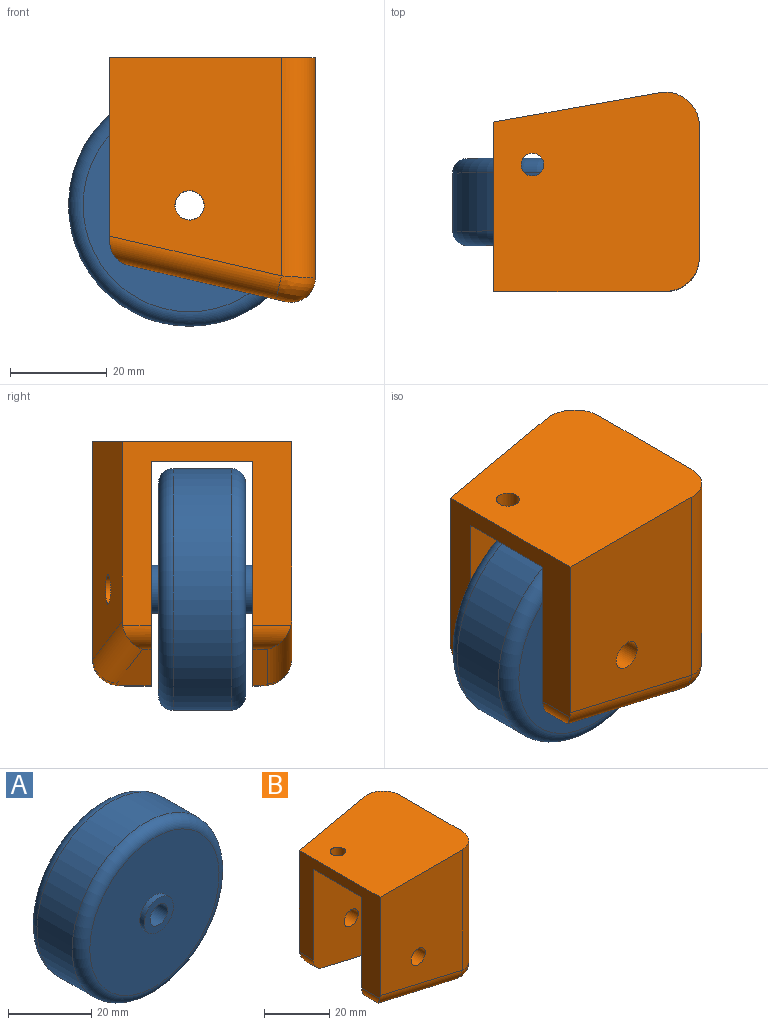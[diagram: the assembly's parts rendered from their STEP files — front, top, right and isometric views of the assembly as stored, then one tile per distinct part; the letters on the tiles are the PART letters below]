
ASSEMBLY  parts=2 mates=1
PART A: 10 faces, bbox 54.1x21x54.1 mm
  f0: cylinder r=25mm len=50mm, axis (0,1,0), area 1885mm2, adj f8,f9
  f1: cylinder r=3mm len=21mm, axis (0,1,0), area 395.8mm2, adj f5,f7
  f2: plane 44x44mm, normal (0,-1,0), area 1442mm2, adj f4,f9
  f3: plane 44x44mm, normal (0,1,0), area 1442mm2, adj f6,f8
  f4: cylinder r=5mm len=10mm, axis (0,1,0), area 47.1mm2, adj f2,f5
  f5: plane 10x10mm, normal (0,-1,0), area 50.3mm2, adj f1,f4
  f6: cylinder r=5mm len=10mm, axis (0,-1,0), area 47.1mm2, adj f3,f7
  f7: plane 10x10mm, normal (0,1,0), area 50.3mm2, adj f1,f6
  f8: torus R=22mm, axis (0,-1,0), area 707.9mm2, adj f0,f3
  f9: torus R=22mm, axis (0,-1,0), area 707.9mm2, adj f0,f2
PART B: 23 faces, bbox 43.9x41.6x52.1 mm
  f0: plane 45.55x27.16mm, normal (1,0,0), area 364.4mm2, adj f1,f3,f4,f5,f6,f10,f15,f19
  f1: cylinder r=7mm len=45.55mm, axis (0,0,-1), area 553.2mm2, adj f0,f2,f10,f16
  f2: plane 45.23x34.51mm, normal (-0.17,0.98,0), area 1398.9mm2, adj f1,f7,f10,f12,f18
  f3: cylinder r=7mm len=45.55mm, axis (0,0,-1), area 498.3mm2, adj f0,f8,f10,f21
  f4: plane 46.55x42.5mm, normal (0,-1,0), area 1782.7mm2, adj f0,f6,f7,f12,f14,f15,f17
  f5: plane 46.55x42.5mm, normal (0,1,0), area 1782.7mm2, adj f0,f6,f7,f11,f13,f19,f20
  f6: plane 42.5x21mm, normal (0,0,-1), area 875.2mm2, adj f0,f4,f5,f7,f9
  f7: plane 38.03x35.01mm, normal (-1,0,0), area 616.3mm2, adj f2,f4,f5,f6,f8,f10,f17,f18
  f8: plane 45.08x35.5mm, normal (0,-1,0), area 1425.4mm2, adj f3,f7,f10,f11,f22
  f9: cylinder r=2.35mm len=4.7mm, axis (0,0,-1), area 59.1mm2, adj f6,f10
  f10: plane 42.5x41.16mm, normal (0,0,1), area 1603.4mm2, adj f0,f1,f2,f3,f7,f8,f9
  f11: cylinder r=3.05mm len=8mm, axis (0,-1,0), area 153.3mm2, adj f5,f8
  f12: cylinder r=3.05mm len=9.45mm, axis (0,-1,0), area 170.8mm2, adj f2,f4
  f13: plane 32.5x7.52mm, normal (-0.23,0,-0.97), area 99.2mm2, adj f5,f19,f20,f21,f22
  f14: plane 32.5x7.52mm, normal (-0.23,0,-0.97), area 154.6mm2, adj f4,f15,f16,f17,f18
  f15: cylinder r=5mm len=6.13mm, axis (0,1,0), area 46.4mm2, adj f0,f4,f14,f16
  f16: bspline ~10.07x7.1mm, area 79.2mm2, adj f1,f14,f15,f18
  f17: cylinder r=5mm len=5.91mm, axis (0,1,0), area 28.4mm2, adj f4,f7,f14,f18
  f18: cylinder r=5mm len=34.81mm, axis (-0.96,-0.17,0.22), area 260.8mm2, adj f2,f7,f14,f16,f17
  f19: cylinder r=5mm len=6.13mm, axis (0,1,0), area 9mm2, adj f0,f5,f13,f21
  f20: cylinder r=5mm len=7.87mm, axis (0,1,0), area 39.5mm2, adj f5,f7,f13,f22
  f21: bspline ~9.27x7.1mm, area 72.2mm2, adj f3,f13,f19,f22
  f22: cylinder r=5mm len=36.63mm, axis (-0.97,0,0.23), area 270.9mm2, adj f7,f8,f13,f20,f21
PLACE A t=(-69.06,28.45,18.86)mm
PLACE B t=(44.66,20.68,24.25)mm
MATE fastened B.f11 <-> A.f0  axis (0,-1,0) through (36.29,8.95,-2.25)mm
